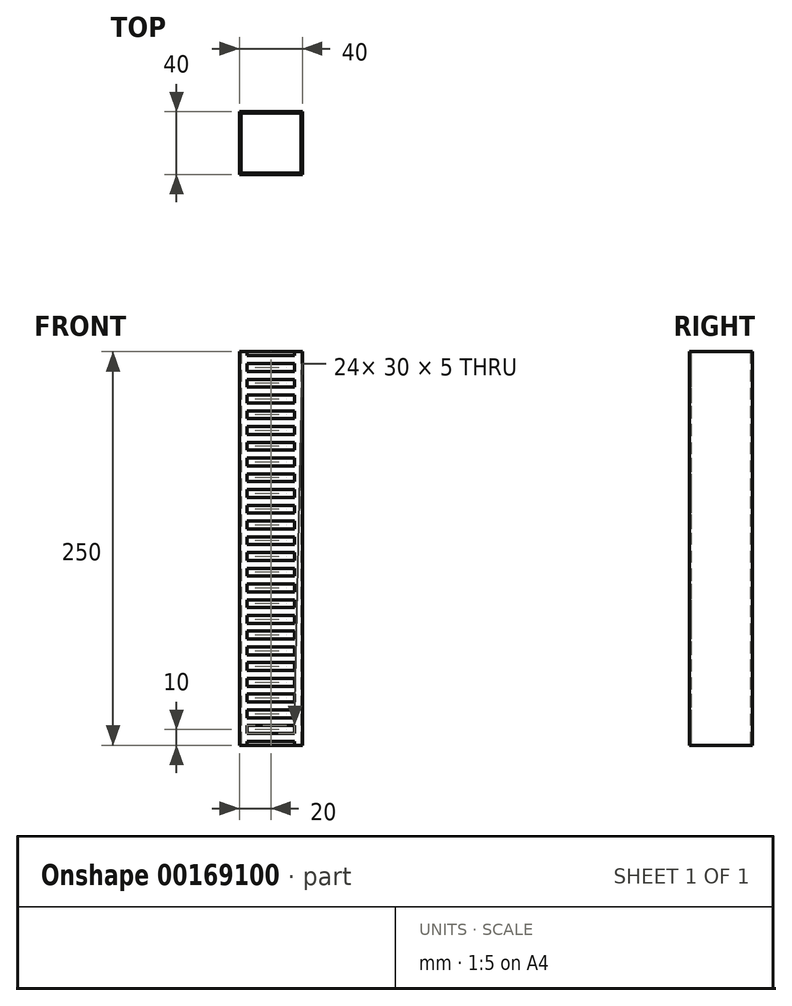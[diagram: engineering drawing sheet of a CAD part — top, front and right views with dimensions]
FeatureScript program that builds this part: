
annotation { "Feature Type Name" : "Feature", "Feature Type Description" : "" }
export const myFeature = defineFeature(function(context is Context, id is Id, definition is map)
    precondition{}
    {
        {
            var Q0;
            Q0=qCreatedBy(makeId("Top.planeOp"),FACE);
            var sketch = newSketch(context, id + "F0", { "sketchPlane" : qUnion([Q0])});
            skLineSegment(sketch, "E0.bottom", {"start": v(20, 20) * mm, "end": v(-20, 20) * mm});
            skLineSegment(sketch, "E0.top", {"start": v(20, -20) * mm, "end": v(-20, -20) * mm});
            skLineSegment(sketch, "E0.left", {"start": v(20, 20) * mm, "end": v(20, -20) * mm});
            skLineSegment(sketch, "E0.right", {"start": v(-20, 20) * mm, "end": v(-20, -20) * mm});
            skPoint(sketch, "E0.middle", {"position": v(0, 0) * mm});
            skLineSegment(sketch, "E1.bottom", {"start": v(19, 19) * mm, "end": v(-19, 19) * mm});
            skLineSegment(sketch, "E1.top", {"start": v(19, -19) * mm, "end": v(-19, -19) * mm});
            skLineSegment(sketch, "E1.left", {"start": v(19, 19) * mm, "end": v(19, -19) * mm});
            skLineSegment(sketch, "E1.right", {"start": v(-19, 19) * mm, "end": v(-19, -19) * mm});
            skSolve(sketch);
        }
        {
            var Q0;
            Q0=makeQuery(id+"F0.imprint","IMPRINT",FACE,{"disambiguationData":[TD([[makeQuery(id+"F0.imprint","IMPRINT",EDGE,{"derivedFrom":sQuery(id+"F0.wireOp",EDGE,"E0.bottom")}),1.0]])]});
            extrude(context, id + "F1", {"entities" : qUnion([Q0]), "depth" : 250 * mm});
        }
        {
            var Q0;
            Q0=makeQuery(id+"F1.opExtrude","SWEPT_FACE",FACE,{"disambiguationData":[OSD([sQuery(id+"F0.wireOp",EDGE,"E0.top")])]});
            var sketch = newSketch(context, id + "F2", { "sketchPlane" : qUnion([Q0])});
            skLineSegment(sketch, "E2.bottom", {"start": v(15, 2.5) * mm, "end": v(-15, 2.5) * mm});
            skLineSegment(sketch, "E2.top", {"start": v(15, -2.5) * mm, "end": v(-15, -2.5) * mm});
            skLineSegment(sketch, "E2.left", {"start": v(15, 2.5) * mm, "end": v(15, -2.5) * mm});
            skLineSegment(sketch, "E2.right", {"start": v(-15, 2.5) * mm, "end": v(-15, -2.5) * mm});
            skPoint(sketch, "E2.middle", {"position": v(0, 0) * mm});
            skLineSegment(sketch, "E3", {"start": v(0, 0) * mm, "end": v(0, 93.34) * mm, "construction": true});
            skLineSegment(sketch, "E4.0.1.0", {"start": v(15, 7.5) * mm, "end": v(-15, 7.5) * mm});
            skLineSegment(sketch, "E4.0.1.1", {"start": v(15, 12.5) * mm, "end": v(-15, 12.5) * mm});
            skLineSegment(sketch, "E4.0.1.2", {"start": v(-15, 12.5) * mm, "end": v(-15, 7.5) * mm});
            skLineSegment(sketch, "E4.0.1.3", {"start": v(15, 12.5) * mm, "end": v(15, 7.5) * mm});
            skLineSegment(sketch, "E4.0.2.0", {"start": v(15, 17.5) * mm, "end": v(-15, 17.5) * mm});
            skLineSegment(sketch, "E4.0.2.1", {"start": v(15, 22.5) * mm, "end": v(-15, 22.5) * mm});
            skLineSegment(sketch, "E4.0.2.2", {"start": v(-15, 22.5) * mm, "end": v(-15, 17.5) * mm});
            skLineSegment(sketch, "E4.0.2.3", {"start": v(15, 22.5) * mm, "end": v(15, 17.5) * mm});
            skLineSegment(sketch, "E4.0.3.0", {"start": v(15, 27.5) * mm, "end": v(-15, 27.5) * mm});
            skLineSegment(sketch, "E4.0.3.1", {"start": v(15, 32.5) * mm, "end": v(-15, 32.5) * mm});
            skLineSegment(sketch, "E4.0.3.2", {"start": v(-15, 32.5) * mm, "end": v(-15, 27.5) * mm});
            skLineSegment(sketch, "E4.0.3.3", {"start": v(15, 32.5) * mm, "end": v(15, 27.5) * mm});
            skLineSegment(sketch, "E4.0.4.0", {"start": v(15, 37.5) * mm, "end": v(-15, 37.5) * mm});
            skLineSegment(sketch, "E4.0.4.1", {"start": v(15, 42.5) * mm, "end": v(-15, 42.5) * mm});
            skLineSegment(sketch, "E4.0.4.2", {"start": v(-15, 42.5) * mm, "end": v(-15, 37.5) * mm});
            skLineSegment(sketch, "E4.0.4.3", {"start": v(15, 42.5) * mm, "end": v(15, 37.5) * mm});
            skLineSegment(sketch, "E4.0.5.0", {"start": v(15, 47.5) * mm, "end": v(-15, 47.5) * mm});
            skLineSegment(sketch, "E4.0.5.1", {"start": v(15, 52.5) * mm, "end": v(-15, 52.5) * mm});
            skLineSegment(sketch, "E4.0.5.2", {"start": v(-15, 52.5) * mm, "end": v(-15, 47.5) * mm});
            skLineSegment(sketch, "E4.0.5.3", {"start": v(15, 52.5) * mm, "end": v(15, 47.5) * mm});
            skLineSegment(sketch, "E4.0.6.0", {"start": v(15, 57.5) * mm, "end": v(-15, 57.5) * mm});
            skLineSegment(sketch, "E4.0.6.1", {"start": v(15, 62.5) * mm, "end": v(-15, 62.5) * mm});
            skLineSegment(sketch, "E4.0.6.2", {"start": v(-15, 62.5) * mm, "end": v(-15, 57.5) * mm});
            skLineSegment(sketch, "E4.0.6.3", {"start": v(15, 62.5) * mm, "end": v(15, 57.5) * mm});
            skLineSegment(sketch, "E4.0.7.0", {"start": v(15, 67.5) * mm, "end": v(-15, 67.5) * mm});
            skLineSegment(sketch, "E4.0.7.1", {"start": v(15, 72.5) * mm, "end": v(-15, 72.5) * mm});
            skLineSegment(sketch, "E4.0.7.2", {"start": v(-15, 72.5) * mm, "end": v(-15, 67.5) * mm});
            skLineSegment(sketch, "E4.0.7.3", {"start": v(15, 72.5) * mm, "end": v(15, 67.5) * mm});
            skLineSegment(sketch, "E4.0.8.0", {"start": v(15, 77.5) * mm, "end": v(-15, 77.5) * mm});
            skLineSegment(sketch, "E4.0.8.1", {"start": v(15, 82.5) * mm, "end": v(-15, 82.5) * mm});
            skLineSegment(sketch, "E4.0.8.2", {"start": v(-15, 82.5) * mm, "end": v(-15, 77.5) * mm});
            skLineSegment(sketch, "E4.0.8.3", {"start": v(15, 82.5) * mm, "end": v(15, 77.5) * mm});
            skLineSegment(sketch, "E4.0.9.0", {"start": v(15, 87.5) * mm, "end": v(-15, 87.5) * mm});
            skLineSegment(sketch, "E4.0.9.1", {"start": v(15, 92.5) * mm, "end": v(-15, 92.5) * mm});
            skLineSegment(sketch, "E4.0.9.2", {"start": v(-15, 92.5) * mm, "end": v(-15, 87.5) * mm});
            skLineSegment(sketch, "E4.0.9.3", {"start": v(15, 92.5) * mm, "end": v(15, 87.5) * mm});
            skLineSegment(sketch, "E4.0.10.0", {"start": v(15, 97.5) * mm, "end": v(-15, 97.5) * mm});
            skLineSegment(sketch, "E4.0.10.1", {"start": v(15, 102.5) * mm, "end": v(-15, 102.5) * mm});
            skLineSegment(sketch, "E4.0.10.2", {"start": v(-15, 102.5) * mm, "end": v(-15, 97.5) * mm});
            skLineSegment(sketch, "E4.0.10.3", {"start": v(15, 102.5) * mm, "end": v(15, 97.5) * mm});
            skLineSegment(sketch, "E4.0.11.0", {"start": v(15, 107.5) * mm, "end": v(-15, 107.5) * mm});
            skLineSegment(sketch, "E4.0.11.1", {"start": v(15, 112.5) * mm, "end": v(-15, 112.5) * mm});
            skLineSegment(sketch, "E4.0.11.2", {"start": v(-15, 112.5) * mm, "end": v(-15, 107.5) * mm});
            skLineSegment(sketch, "E4.0.11.3", {"start": v(15, 112.5) * mm, "end": v(15, 107.5) * mm});
            skLineSegment(sketch, "E4.0.12.0", {"start": v(15, 117.5) * mm, "end": v(-15, 117.5) * mm});
            skLineSegment(sketch, "E4.0.12.1", {"start": v(15, 122.5) * mm, "end": v(-15, 122.5) * mm});
            skLineSegment(sketch, "E4.0.12.2", {"start": v(-15, 122.5) * mm, "end": v(-15, 117.5) * mm});
            skLineSegment(sketch, "E4.0.12.3", {"start": v(15, 122.5) * mm, "end": v(15, 117.5) * mm});
            skLineSegment(sketch, "E4.0.13.0", {"start": v(15, 127.5) * mm, "end": v(-15, 127.5) * mm});
            skLineSegment(sketch, "E4.0.13.1", {"start": v(15, 132.5) * mm, "end": v(-15, 132.5) * mm});
            skLineSegment(sketch, "E4.0.13.2", {"start": v(-15, 132.5) * mm, "end": v(-15, 127.5) * mm});
            skLineSegment(sketch, "E4.0.13.3", {"start": v(15, 132.5) * mm, "end": v(15, 127.5) * mm});
            skLineSegment(sketch, "E4.0.14.0", {"start": v(15, 137.5) * mm, "end": v(-15, 137.5) * mm});
            skLineSegment(sketch, "E4.0.14.1", {"start": v(15, 142.5) * mm, "end": v(-15, 142.5) * mm});
            skLineSegment(sketch, "E4.0.14.2", {"start": v(-15, 142.5) * mm, "end": v(-15, 137.5) * mm});
            skLineSegment(sketch, "E4.0.14.3", {"start": v(15, 142.5) * mm, "end": v(15, 137.5) * mm});
            skLineSegment(sketch, "E4.0.15.0", {"start": v(15, 147.5) * mm, "end": v(-15, 147.5) * mm});
            skLineSegment(sketch, "E4.0.15.1", {"start": v(15, 152.5) * mm, "end": v(-15, 152.5) * mm});
            skLineSegment(sketch, "E4.0.15.2", {"start": v(-15, 152.5) * mm, "end": v(-15, 147.5) * mm});
            skLineSegment(sketch, "E4.0.15.3", {"start": v(15, 152.5) * mm, "end": v(15, 147.5) * mm});
            skLineSegment(sketch, "E4.0.16.0", {"start": v(15, 157.5) * mm, "end": v(-15, 157.5) * mm});
            skLineSegment(sketch, "E4.0.16.1", {"start": v(15, 162.5) * mm, "end": v(-15, 162.5) * mm});
            skLineSegment(sketch, "E4.0.16.2", {"start": v(-15, 162.5) * mm, "end": v(-15, 157.5) * mm});
            skLineSegment(sketch, "E4.0.16.3", {"start": v(15, 162.5) * mm, "end": v(15, 157.5) * mm});
            skLineSegment(sketch, "E4.0.17.0", {"start": v(15, 167.5) * mm, "end": v(-15, 167.5) * mm});
            skLineSegment(sketch, "E4.0.17.1", {"start": v(15, 172.5) * mm, "end": v(-15, 172.5) * mm});
            skLineSegment(sketch, "E4.0.17.2", {"start": v(-15, 172.5) * mm, "end": v(-15, 167.5) * mm});
            skLineSegment(sketch, "E4.0.17.3", {"start": v(15, 172.5) * mm, "end": v(15, 167.5) * mm});
            skLineSegment(sketch, "E4.0.18.0", {"start": v(15, 177.5) * mm, "end": v(-15, 177.5) * mm});
            skLineSegment(sketch, "E4.0.18.1", {"start": v(15, 182.5) * mm, "end": v(-15, 182.5) * mm});
            skLineSegment(sketch, "E4.0.18.2", {"start": v(-15, 182.5) * mm, "end": v(-15, 177.5) * mm});
            skLineSegment(sketch, "E4.0.18.3", {"start": v(15, 182.5) * mm, "end": v(15, 177.5) * mm});
            skLineSegment(sketch, "E4.0.19.0", {"start": v(15, 187.5) * mm, "end": v(-15, 187.5) * mm});
            skLineSegment(sketch, "E4.0.19.1", {"start": v(15, 192.5) * mm, "end": v(-15, 192.5) * mm});
            skLineSegment(sketch, "E4.0.19.2", {"start": v(-15, 192.5) * mm, "end": v(-15, 187.5) * mm});
            skLineSegment(sketch, "E4.0.19.3", {"start": v(15, 192.5) * mm, "end": v(15, 187.5) * mm});
            skLineSegment(sketch, "E4.0.20.0", {"start": v(15, 197.5) * mm, "end": v(-15, 197.5) * mm});
            skLineSegment(sketch, "E4.0.20.1", {"start": v(15, 202.5) * mm, "end": v(-15, 202.5) * mm});
            skLineSegment(sketch, "E4.0.20.2", {"start": v(-15, 202.5) * mm, "end": v(-15, 197.5) * mm});
            skLineSegment(sketch, "E4.0.20.3", {"start": v(15, 202.5) * mm, "end": v(15, 197.5) * mm});
            skLineSegment(sketch, "E4.0.21.0", {"start": v(15, 207.5) * mm, "end": v(-15, 207.5) * mm});
            skLineSegment(sketch, "E4.0.21.1", {"start": v(15, 212.5) * mm, "end": v(-15, 212.5) * mm});
            skLineSegment(sketch, "E4.0.21.2", {"start": v(-15, 212.5) * mm, "end": v(-15, 207.5) * mm});
            skLineSegment(sketch, "E4.0.21.3", {"start": v(15, 212.5) * mm, "end": v(15, 207.5) * mm});
            skLineSegment(sketch, "E4.0.22.0", {"start": v(15, 217.5) * mm, "end": v(-15, 217.5) * mm});
            skLineSegment(sketch, "E4.0.22.1", {"start": v(15, 222.5) * mm, "end": v(-15, 222.5) * mm});
            skLineSegment(sketch, "E4.0.22.2", {"start": v(-15, 222.5) * mm, "end": v(-15, 217.5) * mm});
            skLineSegment(sketch, "E4.0.22.3", {"start": v(15, 222.5) * mm, "end": v(15, 217.5) * mm});
            skLineSegment(sketch, "E4.0.23.0", {"start": v(15, 227.5) * mm, "end": v(-15, 227.5) * mm});
            skLineSegment(sketch, "E4.0.23.1", {"start": v(15, 232.5) * mm, "end": v(-15, 232.5) * mm});
            skLineSegment(sketch, "E4.0.23.2", {"start": v(-15, 232.5) * mm, "end": v(-15, 227.5) * mm});
            skLineSegment(sketch, "E4.0.23.3", {"start": v(15, 232.5) * mm, "end": v(15, 227.5) * mm});
            skLineSegment(sketch, "E4.0.24.0", {"start": v(15, 237.5) * mm, "end": v(-15, 237.5) * mm});
            skLineSegment(sketch, "E4.0.24.1", {"start": v(15, 242.5) * mm, "end": v(-15, 242.5) * mm});
            skLineSegment(sketch, "E4.0.24.2", {"start": v(-15, 242.5) * mm, "end": v(-15, 237.5) * mm});
            skLineSegment(sketch, "E4.0.24.3", {"start": v(15, 242.5) * mm, "end": v(15, 237.5) * mm});
            skLineSegment(sketch, "E4.0.25.0", {"start": v(15, 247.5) * mm, "end": v(-15, 247.5) * mm});
            skLineSegment(sketch, "E4.0.25.1", {"start": v(15, 252.5) * mm, "end": v(-15, 252.5) * mm});
            skLineSegment(sketch, "E4.0.25.2", {"start": v(-15, 252.5) * mm, "end": v(-15, 247.5) * mm});
            skLineSegment(sketch, "E4.0.25.3", {"start": v(15, 252.5) * mm, "end": v(15, 247.5) * mm});
            skLineSegment(sketch, "E4.0.26.0", {"start": v(15, 257.5) * mm, "end": v(-15, 257.5) * mm});
            skLineSegment(sketch, "E4.0.26.1", {"start": v(15, 262.5) * mm, "end": v(-15, 262.5) * mm});
            skLineSegment(sketch, "E4.0.26.2", {"start": v(-15, 262.5) * mm, "end": v(-15, 257.5) * mm});
            skLineSegment(sketch, "E4.0.26.3", {"start": v(15, 262.5) * mm, "end": v(15, 257.5) * mm});
            skLineSegment(sketch, "E4.0.27.0", {"start": v(15, 267.5) * mm, "end": v(-15, 267.5) * mm});
            skLineSegment(sketch, "E4.0.27.1", {"start": v(15, 272.5) * mm, "end": v(-15, 272.5) * mm});
            skLineSegment(sketch, "E4.0.27.2", {"start": v(-15, 272.5) * mm, "end": v(-15, 267.5) * mm});
            skLineSegment(sketch, "E4.0.27.3", {"start": v(15, 272.5) * mm, "end": v(15, 267.5) * mm});
            skLineSegment(sketch, "E4.0.28.0", {"start": v(15, 277.5) * mm, "end": v(-15, 277.5) * mm});
            skLineSegment(sketch, "E4.0.28.1", {"start": v(15, 282.5) * mm, "end": v(-15, 282.5) * mm});
            skLineSegment(sketch, "E4.0.28.2", {"start": v(-15, 282.5) * mm, "end": v(-15, 277.5) * mm});
            skLineSegment(sketch, "E4.0.28.3", {"start": v(15, 282.5) * mm, "end": v(15, 277.5) * mm});
            skLineSegment(sketch, "E4.0.29.0", {"start": v(15, 287.5) * mm, "end": v(-15, 287.5) * mm});
            skLineSegment(sketch, "E4.0.29.1", {"start": v(15, 292.5) * mm, "end": v(-15, 292.5) * mm});
            skLineSegment(sketch, "E4.0.29.2", {"start": v(-15, 292.5) * mm, "end": v(-15, 287.5) * mm});
            skLineSegment(sketch, "E4.0.29.3", {"start": v(15, 292.5) * mm, "end": v(15, 287.5) * mm});
            skLineSegment(sketch, "E4.direction1", {"start": v(-15, -2.5) * mm, "end": v(-40, -2.5) * mm, "construction": true});
            skLineSegment(sketch, "E4.direction2", {"start": v(-15, -2.5) * mm, "end": v(-15, 7.5) * mm, "construction": true});
            skSolve(sketch);
        }
        {
            var Q0;
            Q0 = qSketchRegion(id + "F2", true);
            extrude(context, id + "F3", {"entities" : qUnion([Q0]), "operationType" : NewBodyOperationType.REMOVE, "oppositeDirection" : true, "depth" : 25 * mm});
        }
    });
